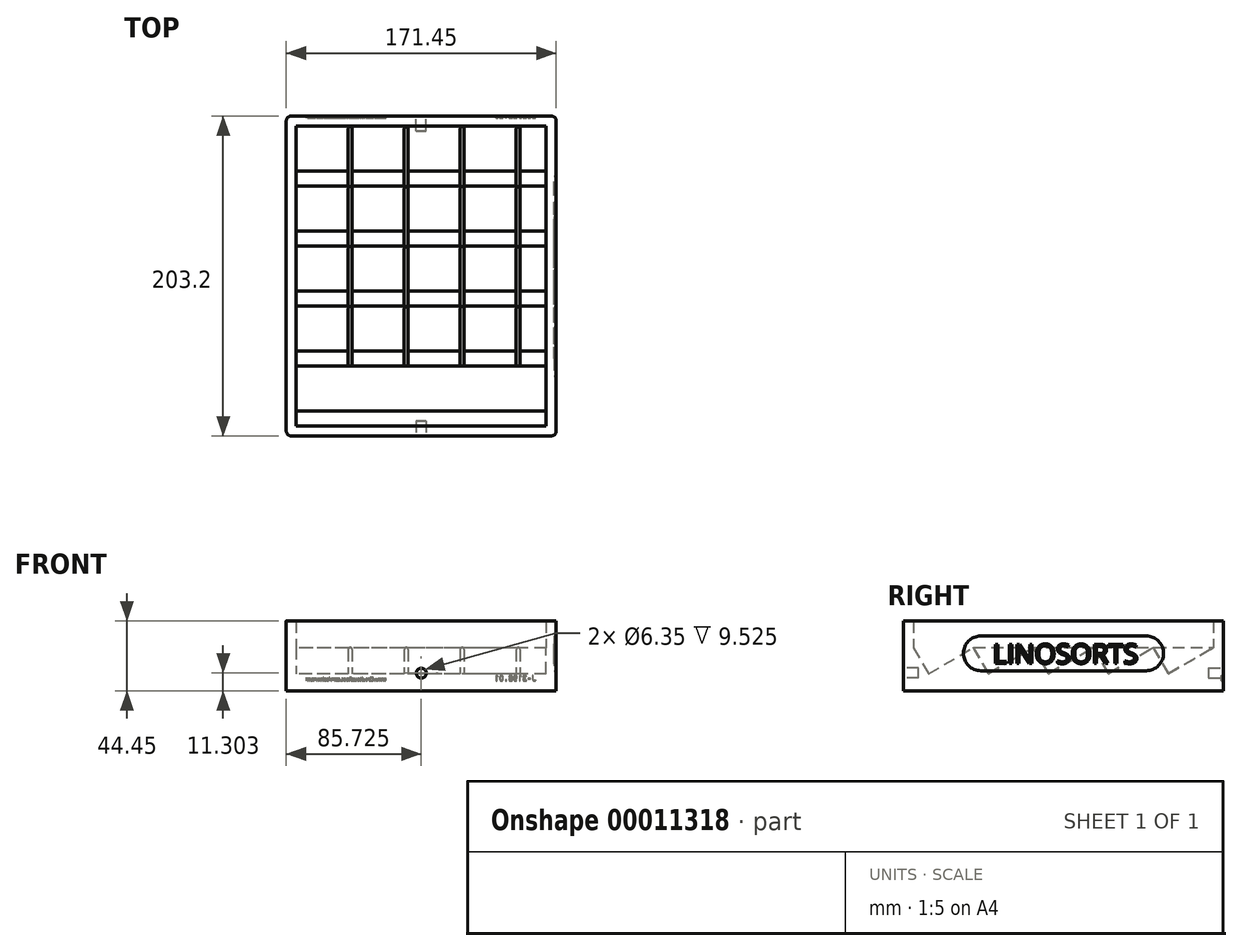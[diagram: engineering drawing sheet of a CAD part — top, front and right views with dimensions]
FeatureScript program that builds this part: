
annotation { "Feature Type Name" : "Feature", "Feature Type Description" : "" }
export const myFeature = defineFeature(function(context is Context, id is Id, definition is map)
    precondition{}
    {
        {
            var Q0;
            Q0=qCreatedBy(makeId("Top.planeOp"),FACE);
            var sketch = newSketch(context, id + "F0", { "sketchPlane" : qUnion([Q0])});
            skLineSegment(sketch, "E0.bottom", {"start": v(3.17, 0) * mm, "end": v(168.28, 0) * mm});
            skLineSegment(sketch, "E0.top", {"start": v(3.17, 203.2) * mm, "end": v(168.27, 203.2) * mm});
            skLineSegment(sketch, "E0.left", {"start": v(0, 3.18) * mm, "end": v(0, 200.03) * mm});
            skLineSegment(sketch, "E0.right", {"start": v(171.45, 3.18) * mm, "end": v(171.45, 200.03) * mm});
            skPoint(sketch, "E1.visualSharp", {"position": v(0, 203.2) * mm});
            skArc(sketch, "E1.filletArc", {"start": v(3.17, 203.2) * mm, "mid": v(0.93, 202.27) * mm, "end": v(0, 200.03) * mm});
            skPoint(sketch, "E2.visualSharp", {"position": v(171.45, 203.2) * mm});
            skArc(sketch, "E2.filletArc", {"start": v(171.45, 200.03) * mm, "mid": v(170.52, 202.27) * mm, "end": v(168.27, 203.2) * mm});
            skPoint(sketch, "E3.visualSharp", {"position": v(171.45, 0) * mm});
            skArc(sketch, "E3.filletArc", {"start": v(168.28, 0) * mm, "mid": v(170.52, 0.93) * mm, "end": v(171.45, 3.18) * mm});
            skPoint(sketch, "E4.visualSharp", {"position": v(0, 0) * mm});
            skArc(sketch, "E4.filletArc", {"start": v(0, 3.18) * mm, "mid": v(0.93, 0.93) * mm, "end": v(3.17, 0) * mm});
            skSolve(sketch);
        }
        {
            var Q0;
            Q0 = qSketchRegion(id + "F0", true);
            extrude(context, id + "F1", {"entities" : qUnion([Q0]), "depth" : 9.52 * mm});
        }
        {
            var Q0;
            Q0=makeQuery(id+"F1.opExtrude","CAP_FACE",FACE,{"disambiguationData":[OSD([sQuery(id+"F0.wireOp",EDGE,"E0.bottom"),sQuery(id+"F0.wireOp",EDGE,"E0.top"),sQuery(id+"F0.wireOp",EDGE,"E0.left"),sQuery(id+"F0.wireOp",EDGE,"E0.right"),sQuery(id+"F0.wireOp",EDGE,"E1.filletArc"),sQuery(id+"F0.wireOp",EDGE,"E2.filletArc"),sQuery(id+"F0.wireOp",EDGE,"E3.filletArc"),sQuery(id+"F0.wireOp",EDGE,"E4.filletArc")])],"isStart":false});
            var sketch = newSketch(context, id + "F2", { "sketchPlane" : qUnion([Q0])});
            skArc(sketch, "E5.0", {"start": v(3.17, 203.2) * mm, "mid": v(0.93, 202.27) * mm, "end": v(0, 200.03) * mm});
            skArc(sketch, "E6.0", {"start": v(171.45, 200.03) * mm, "mid": v(170.52, 202.27) * mm, "end": v(168.27, 203.2) * mm});
            skArc(sketch, "E7.0", {"start": v(0, 3.18) * mm, "mid": v(0.93, 0.93) * mm, "end": v(3.17, 0) * mm});
            skArc(sketch, "E8.0", {"start": v(168.28, 0) * mm, "mid": v(170.52, 0.93) * mm, "end": v(171.45, 3.18) * mm});
            skLineSegment(sketch, "E9.0", {"start": v(3.17, 203.2) * mm, "end": v(168.27, 203.2) * mm});
            skLineSegment(sketch, "E10.0", {"start": v(0, 3.18) * mm, "end": v(0, 200.03) * mm});
            skLineSegment(sketch, "E11.0", {"start": v(171.45, 3.18) * mm, "end": v(171.45, 200.03) * mm});
            skLineSegment(sketch, "E12.0", {"start": v(3.17, 0) * mm, "end": v(168.28, 0) * mm});
            skLineSegment(sketch, "E13.bottom", {"start": v(6.35, 196.85) * mm, "end": v(165.1, 196.85) * mm});
            skLineSegment(sketch, "E13.top", {"start": v(6.35, 6.35) * mm, "end": v(165.1, 6.35) * mm});
            skLineSegment(sketch, "E13.left", {"start": v(6.35, 196.85) * mm, "end": v(6.35, 6.35) * mm});
            skLineSegment(sketch, "E13.right", {"start": v(165.1, 196.85) * mm, "end": v(165.1, 6.35) * mm});
            skSolve(sketch);
        }
        {
            var Q0;
            Q0 = qSketchRegion(id + "F2", true);
            extrude(context, id + "F3", {"entities" : qUnion([Q0]), "operationType" : NewBodyOperationType.ADD, "depth" : 34.92 * mm});
        }
        {
            var Q0;
            Q0=makeQuery(id+"F1.opExtrude","CAP_FACE",FACE,{"disambiguationData":[OSD([sQuery(id+"F0.wireOp",EDGE,"E0.bottom"),sQuery(id+"F0.wireOp",EDGE,"E0.top"),sQuery(id+"F0.wireOp",EDGE,"E0.left"),sQuery(id+"F0.wireOp",EDGE,"E0.right"),sQuery(id+"F0.wireOp",EDGE,"E1.filletArc"),sQuery(id+"F0.wireOp",EDGE,"E2.filletArc"),sQuery(id+"F0.wireOp",EDGE,"E3.filletArc"),sQuery(id+"F0.wireOp",EDGE,"E4.filletArc")])],"isStart":false});
            var sketch = newSketch(context, id + "F4", { "sketchPlane" : qUnion([Q0])});
            skLineSegment(sketch, "E14.bottom", {"start": v(39.37, 196.85) * mm, "end": v(41.9, 196.85) * mm});
            skLineSegment(sketch, "E14.top", {"start": v(39.37, 44.45) * mm, "end": v(41.91, 44.45) * mm});
            skLineSegment(sketch, "E14.left", {"start": v(39.37, 196.85) * mm, "end": v(39.37, 44.45) * mm});
            skLineSegment(sketch, "E14.right", {"start": v(41.9, 196.85) * mm, "end": v(41.91, 44.45) * mm});
            skLineSegment(sketch, "E15.1.0.0", {"start": v(74.93, 196.85) * mm, "end": v(77.47, 196.85) * mm});
            skLineSegment(sketch, "E15.1.0.1", {"start": v(74.93, 196.85) * mm, "end": v(74.93, 44.45) * mm});
            skLineSegment(sketch, "E15.1.0.2", {"start": v(77.47, 196.85) * mm, "end": v(77.47, 44.45) * mm});
            skLineSegment(sketch, "E15.1.0.3", {"start": v(74.93, 44.45) * mm, "end": v(77.47, 44.45) * mm});
            skLineSegment(sketch, "E15.2.0.0", {"start": v(110.5, 196.85) * mm, "end": v(113.03, 196.85) * mm});
            skLineSegment(sketch, "E15.2.0.1", {"start": v(110.5, 196.85) * mm, "end": v(110.5, 44.45) * mm});
            skLineSegment(sketch, "E15.2.0.2", {"start": v(113.03, 196.85) * mm, "end": v(113.03, 44.45) * mm});
            skLineSegment(sketch, "E15.2.0.3", {"start": v(110.5, 44.45) * mm, "end": v(113.03, 44.45) * mm});
            skLineSegment(sketch, "E15.3.0.0", {"start": v(146.05, 196.85) * mm, "end": v(148.6, 196.85) * mm});
            skLineSegment(sketch, "E15.3.0.1", {"start": v(146.05, 196.85) * mm, "end": v(146.05, 44.45) * mm});
            skLineSegment(sketch, "E15.3.0.2", {"start": v(148.6, 196.85) * mm, "end": v(148.6, 44.45) * mm});
            skLineSegment(sketch, "E15.3.0.3", {"start": v(146.05, 44.45) * mm, "end": v(148.6, 44.45) * mm});
            skSolve(sketch);
        }
        {
            var Q0;
            Q0 = qSketchRegion(id + "F4", true);
            extrude(context, id + "F5", {"entities" : qUnion([Q0]), "operationType" : NewBodyOperationType.ADD, "depth" : 18.03 * mm});
        }
        {
            var Q0;
            Q0=makeQuery(id+"F5.opExtrude","CAP_EDGE",EDGE,{"disambiguationData":[OSD([sQuery(id+"F4.wireOp",EDGE,"E14.left")])],"isStart":false});
            var Q1;
            Q1=makeQuery(id+"F5.opExtrude","CAP_EDGE",EDGE,{"disambiguationData":[OSD([sQuery(id+"F4.wireOp",EDGE,"E14.right")])],"isStart":false});
            var Q2;
            Q2=makeQuery(id+"F5.opExtrude","CAP_EDGE",EDGE,{"disambiguationData":[OSD([sQuery(id+"F4.wireOp",EDGE,"E15.1.0.1")])],"isStart":false});
            var Q3;
            Q3=makeQuery(id+"F5.opExtrude","CAP_EDGE",EDGE,{"disambiguationData":[OSD([sQuery(id+"F4.wireOp",EDGE,"E15.1.0.2")])],"isStart":false});
            var Q4;
            Q4=makeQuery(id+"F5.opExtrude","CAP_EDGE",EDGE,{"disambiguationData":[OSD([sQuery(id+"F4.wireOp",EDGE,"E15.2.0.1")])],"isStart":false});
            var Q5;
            Q5=makeQuery(id+"F5.opExtrude","CAP_EDGE",EDGE,{"disambiguationData":[OSD([sQuery(id+"F4.wireOp",EDGE,"E15.2.0.2")])],"isStart":false});
            var Q6;
            Q6=makeQuery(id+"F5.opExtrude","CAP_EDGE",EDGE,{"disambiguationData":[OSD([sQuery(id+"F4.wireOp",EDGE,"E15.3.0.1")])],"isStart":false});
            var Q7;
            Q7=makeQuery(id+"F5.opExtrude","CAP_EDGE",EDGE,{"disambiguationData":[OSD([sQuery(id+"F4.wireOp",EDGE,"E15.3.0.2")])],"isStart":false});
            fillet(context, id + "F6", {"entities" : qUnion([Q0, Q1, Q2, Q3, Q4, Q5, Q6, Q7]), "radius" : 1.27 * mm, "allowEdgeOverflow" : false});
        }
        {
            var Q0;
            Q0=makeQuery(id+"F3.opExtrude","SWEPT_FACE",FACE,{"disambiguationData":[OSD([sQuery(id+"F2.wireOp",EDGE,"E13.left")])]});
            var sketch = newSketch(context, id + "F7", { "sketchPlane" : qUnion([Q0])});
            skLineSegment(sketch, "E16", {"start": v(6.35, 27.43) * mm, "end": v(15.88, 10.93) * mm});
            skLineSegment(sketch, "E17", {"start": v(15.88, 10.93) * mm, "end": v(44.45, 27.43) * mm});
            skLineSegment(sketch, "E18.1.0.0", {"start": v(44.45, 27.43) * mm, "end": v(53.98, 10.93) * mm});
            skLineSegment(sketch, "E18.1.0.1", {"start": v(53.98, 10.93) * mm, "end": v(82.55, 27.43) * mm});
            skLineSegment(sketch, "E18.2.0.0", {"start": v(82.55, 27.43) * mm, "end": v(92.08, 10.93) * mm});
            skLineSegment(sketch, "E18.2.0.1", {"start": v(92.08, 10.93) * mm, "end": v(120.65, 27.43) * mm});
            skLineSegment(sketch, "E18.3.0.0", {"start": v(120.65, 27.43) * mm, "end": v(130.18, 10.93) * mm});
            skLineSegment(sketch, "E18.3.0.1", {"start": v(130.18, 10.93) * mm, "end": v(158.75, 27.43) * mm});
            skLineSegment(sketch, "E18.4.0.0", {"start": v(158.75, 27.43) * mm, "end": v(168.28, 10.93) * mm});
            skLineSegment(sketch, "E18.4.0.1", {"start": v(168.28, 10.93) * mm, "end": v(196.85, 27.43) * mm});
            skLineSegment(sketch, "E18.direction1", {"start": v(15.88, 10.93) * mm, "end": v(53.98, 10.93) * mm, "construction": true});
            skLineSegment(sketch, "E19", {"start": v(6.35, 27.43) * mm, "end": v(6.35, 9.53) * mm});
            skLineSegment(sketch, "E20", {"start": v(6.35, 9.53) * mm, "end": v(196.85, 9.53) * mm});
            skLineSegment(sketch, "E21", {"start": v(196.85, 9.53) * mm, "end": v(196.85, 27.43) * mm});
            skSolve(sketch);
        }
        {
            var Q0;
            Q0 = qSketchRegion(id + "F7", true);
            extrude(context, id + "F8", {"entities" : qUnion([Q0]), "operationType" : NewBodyOperationType.ADD, "endBound" : BoundingType.UP_TO_NEXT, "depth" : 25.4 * mm});
        }
        {
            var Q0;
            Q0=makeQuery(id+"F3.boolean.opBoolean","MERGE",FACE,{"derivedFrom":[makeQuery(id+"F1.opExtrude","SWEPT_FACE",FACE,{"disambiguationData":[OSD([sQuery(id+"F0.wireOp",EDGE,"E0.bottom")])]}),makeQuery(id+"F3.opExtrude","SWEPT_FACE",FACE,{"disambiguationData":[OSD([sQuery(id+"F2.wireOp",EDGE,"E12.0")])]})]});
            var sketch = newSketch(context, id + "F9", { "sketchPlane" : qUnion([Q0])});
            skCircle(sketch, "E22", {"center": v(85.73, 11.3) * mm, "radius": 3.18 * mm});
            skSolve(sketch);
        }
        {
            var Q0;
            Q0 = qSketchRegion(id + "F9", true);
            extrude(context, id + "F10", {"entities" : qUnion([Q0]), "operationType" : NewBodyOperationType.REMOVE, "oppositeDirection" : true, "depth" : 9.52 * mm});
        }
        {
            var Q0;
            Q0=makeQuery(id+"F3.boolean.opBoolean","MERGE",FACE,{"derivedFrom":[makeQuery(id+"F1.opExtrude","SWEPT_FACE",FACE,{"disambiguationData":[OSD([sQuery(id+"F0.wireOp",EDGE,"E0.top")])]}),makeQuery(id+"F3.opExtrude","SWEPT_FACE",FACE,{"disambiguationData":[OSD([sQuery(id+"F2.wireOp",EDGE,"E9.0")])]})]});
            var sketch = newSketch(context, id + "F11", { "sketchPlane" : qUnion([Q0])});
            skCircle(sketch, "E23", {"center": v(-85.72, 11.3) * mm, "radius": 3.18 * mm});
            skSolve(sketch);
        }
        {
            var Q0;
            Q0 = qSketchRegion(id + "F11", true);
            extrude(context, id + "F12", {"entities" : qUnion([Q0]), "operationType" : NewBodyOperationType.REMOVE, "oppositeDirection" : true, "depth" : 9.52 * mm});
        }
        {
            var Q0;
            Q0=makeQuery(id+"F3.boolean.opBoolean","MERGE",FACE,{"derivedFrom":[makeQuery(id+"F1.opExtrude","SWEPT_FACE",FACE,{"disambiguationData":[OSD([sQuery(id+"F0.wireOp",EDGE,"E0.right")])]}),makeQuery(id+"F3.opExtrude","SWEPT_FACE",FACE,{"disambiguationData":[OSD([sQuery(id+"F2.wireOp",EDGE,"E11.0")])]})]});
            var sketch = newSketch(context, id + "F13", { "sketchPlane" : qUnion([Q0])});
            skLineSegment(sketch, "E24.bottom", {"start": v(49.1, 34.83) * mm, "end": v(154.1, 34.83) * mm});
            skLineSegment(sketch, "E24.top", {"start": v(49.1, 12.84) * mm, "end": v(154.1, 12.84) * mm});
            skLineSegment(sketch, "E24.left", {"start": v(38.1, 23.84) * mm, "end": v(38.1, 23.84) * mm});
            skLineSegment(sketch, "E24.right", {"start": v(165.1, 23.84) * mm, "end": v(165.1, 23.84) * mm});
            skPoint(sketch, "E25.visualSharp", {"position": v(38.1, 34.83) * mm});
            skArc(sketch, "E25.filletArc", {"start": v(49.1, 34.83) * mm, "mid": v(41.32, 31.61) * mm, "end": v(38.1, 23.84) * mm});
            skPoint(sketch, "E26.visualSharp", {"position": v(38.1, 12.84) * mm});
            skArc(sketch, "E26.filletArc", {"start": v(38.1, 23.84) * mm, "mid": v(41.32, 16.06) * mm, "end": v(49.1, 12.84) * mm});
            skPoint(sketch, "E27.visualSharp", {"position": v(165.1, 34.83) * mm});
            skArc(sketch, "E27.filletArc", {"start": v(165.1, 23.84) * mm, "mid": v(161.88, 31.61) * mm, "end": v(154.1, 34.83) * mm});
            skPoint(sketch, "E28.visualSharp", {"position": v(165.1, 12.84) * mm});
            skArc(sketch, "E28.filletArc", {"start": v(154.1, 12.84) * mm, "mid": v(161.88, 16.06) * mm, "end": v(165.1, 23.84) * mm});
            skSolve(sketch);
        }
        {
            var Q0;
            Q0 = qSketchRegion(id + "F13", true);
            extrude(context, id + "F14", {"entities" : qUnion([Q0]), "operationType" : NewBodyOperationType.REMOVE, "oppositeDirection" : true, "depth" : 1.27 * mm});
        }
        {
            var Q0;
            Q0=makeQuery(id+"F14.boolean.opBoolean","COPY",FACE,{"derivedFrom":makeQuery(id+"F14.opExtrude","CAP_FACE",FACE,{"disambiguationData":[OSD([sQuery(id+"F13.wireOp",EDGE,"E24.bottom"),sQuery(id+"F13.wireOp",EDGE,"E24.top"),sQuery(id+"F13.wireOp",EDGE,"E25.filletArc"),sQuery(id+"F13.wireOp",EDGE,"E26.filletArc"),sQuery(id+"F13.wireOp",EDGE,"E27.filletArc"),sQuery(id+"F13.wireOp",EDGE,"E28.filletArc")])],"isStart":false})});
            var sketch = newSketch(context, id + "F15", { "sketchPlane" : qUnion([Q0])});
            skText(sketch, "E29", { "text": "LINOSORTS", "fontName": "OpenSans-Regular.ttf"});
            const initialGuessF15  = {"E29": [0.05672, 0.0174, 1, 0, 0.01235]};
            skSetInitialGuess(sketch, initialGuessF15);
            skSolve(sketch);
        }
        {
            var Q0;
            Q0 = qSketchRegion(id + "F15", true);
            extrude(context, id + "F16", {"entities" : qUnion([Q0]), "operationType" : NewBodyOperationType.ADD, "depth" : 1.27 * mm});
        }
        {
            var Q0;
            Q0=makeQuery(id+"F3.boolean.opBoolean","MERGE",FACE,{"derivedFrom":[makeQuery(id+"F1.opExtrude","SWEPT_FACE",FACE,{"disambiguationData":[OSD([sQuery(id+"F0.wireOp",EDGE,"E0.top")])]}),makeQuery(id+"F3.opExtrude","SWEPT_FACE",FACE,{"disambiguationData":[OSD([sQuery(id+"F2.wireOp",EDGE,"E9.0")])]})]});
            var sketch = newSketch(context, id + "F17", { "sketchPlane" : qUnion([Q0])});
            skText(sketch, "E30", { "text": "www.CircuitousRoot.com/oshw.html", "fontName": "OpenSans-Regular.ttf"});
            const initialGuessF17  = {"E30": [-0.0635, 0.00635, 1, 0, 0.00216]};
            skSetInitialGuess(sketch, initialGuessF17);
            skSolve(sketch);
        }
        {
            var Q0;
            Q0 = qSketchRegion(id + "F17", true);
            extrude(context, id + "F18", {"entities" : qUnion([Q0]), "operationType" : NewBodyOperationType.REMOVE, "oppositeDirection" : true, "depth" : 1.27 * mm});
        }
        {
            var Q0;
            Q0=makeQuery(id+"F3.boolean.opBoolean","MERGE",FACE,{"derivedFrom":[makeQuery(id+"F1.opExtrude","SWEPT_FACE",FACE,{"disambiguationData":[OSD([sQuery(id+"F0.wireOp",EDGE,"E0.top")])]}),makeQuery(id+"F3.opExtrude","SWEPT_FACE",FACE,{"disambiguationData":[OSD([sQuery(id+"F2.wireOp",EDGE,"E9.0")])]})]});
            var sketch = newSketch(context, id + "F19", { "sketchPlane" : qUnion([Q0])});
            skText(sketch, "E31", { "text": "J-3198.01", "fontName": "DroidSansMono.ttf"});
            const initialGuessF19  = {"E31": [-0.15875, 0.00635, 1, 0, 0.00354]};
            skSetInitialGuess(sketch, initialGuessF19);
            skSolve(sketch);
        }
        {
            var Q0;
            Q0 = qSketchRegion(id + "F19", true);
            extrude(context, id + "F20", {"entities" : qUnion([Q0]), "operationType" : NewBodyOperationType.REMOVE, "oppositeDirection" : true, "depth" : 1.27 * mm});
        }
    });
